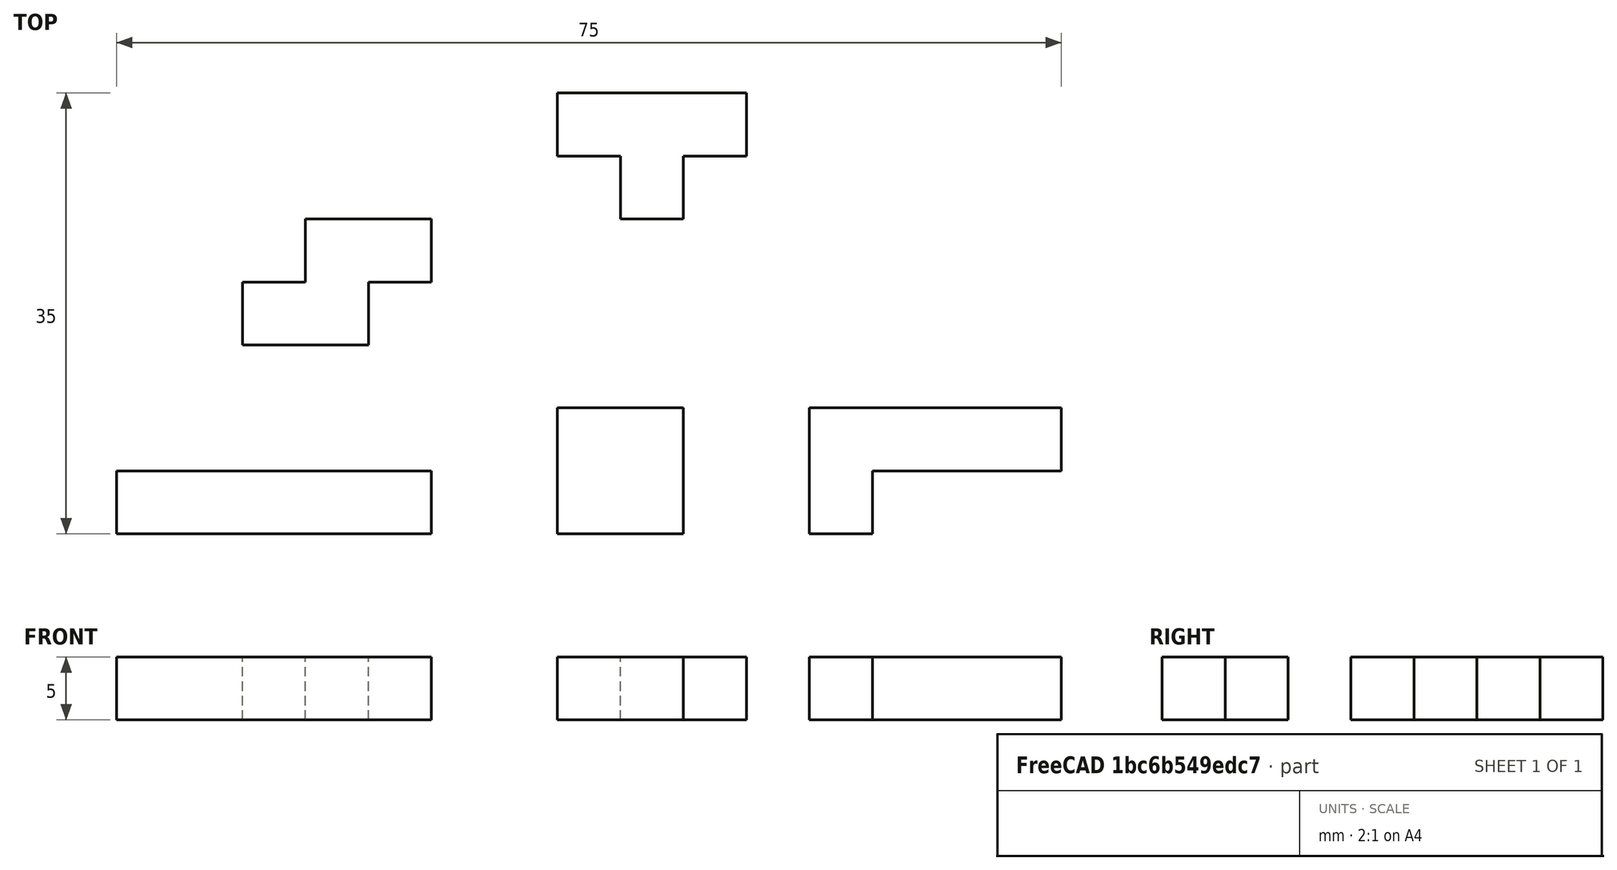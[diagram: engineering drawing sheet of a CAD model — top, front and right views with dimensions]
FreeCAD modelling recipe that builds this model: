
FCSTD DOCUMENT  (FreeCAD 1.0R39319 (Git))
Label: ojt1_t05r03_tetris
License: All rights reserved
LicenseURL: https://en.wikipedia.org/wiki/All_rights_reserved
objects: Part::Box×9, Part::MultiFuse×4
note: 13 computed .brp shape members not serialized (recipe doc carries the construction recipe); baked Part::Feature solids carry a one-line shape summary decoded from their .brp

FEATURE [Part::Box] Box  label="Cub"
  AttacherType = Attacher::AttachEngine3D
  Height = 5
  Length = 10
  Width = 10
FEATURE [Part::Box] Box001  label="Cub001"
  AttacherType = Attacher::AttachEngine3D
  Height = 5
  Length = 25
  Placement = pos=(-35,0,0) rot=(0,0,1;0rad)
  Width = 5
FEATURE [Part::Box] Box002  label="Cub002"
  AttacherType = Attacher::AttachEngine3D
  Height = 5
  Length = 20
  Placement = pos=(-35,0,0) rot=(0,0,1;0rad)
  Width = 5
FEATURE [Part::Box] Box003  label="Cub003"
  AttacherType = Attacher::AttachEngine3D
  Height = 5
  Length = 20
  Placement = pos=(20,5,0) rot=(0,0,1;0rad)
  Width = 5
FEATURE [Part::Box] Box004  label="Cub004"
  AttacherType = Attacher::AttachEngine3D
  Height = 5
  Length = 5
  Placement = pos=(20,0,0) rot=(0,0,1;0rad)
  Width = 5
FEATURE [Part::MultiFuse] Fusion
  Refine = true
  Shapes = -> [Box003,Box004]
FEATURE [Part::Box] Box005  label="Cub005"
  AttacherType = Attacher::AttachEngine3D
  Height = 5
  Length = 15
  Placement = pos=(0,30,0) rot=(0,0,1;0rad)
  Width = 5
FEATURE [Part::Box] Box006  label="Cub006"
  AttacherType = Attacher::AttachEngine3D
  Height = 5
  Length = 5
  Placement = pos=(5,25,0) rot=(0,0,1;0rad)
  Width = 5
FEATURE [Part::MultiFuse] Fusion001
  Refine = true
  Shapes = -> [Box006,Box005]
FEATURE [Part::MultiFuse] Fusion002
  Refine = true
  Shapes = -> [Box001,Box002]
FEATURE [Part::Box] Box007  label="Cub007"
  AttacherType = Attacher::AttachEngine3D
  Height = 5
  Length = 10
  Placement = pos=(-25,15,0) rot=(0,0,1;0rad)
  Width = 5
FEATURE [Part::Box] Box008  label="Cub008"
  AttacherType = Attacher::AttachEngine3D
  Height = 5
  Length = 10
  Placement = pos=(-20,20,0) rot=(0,0,1;0rad)
  Width = 5
FEATURE [Part::MultiFuse] Fusion003
  Refine = true
  Shapes = -> [Box008,Box007]
